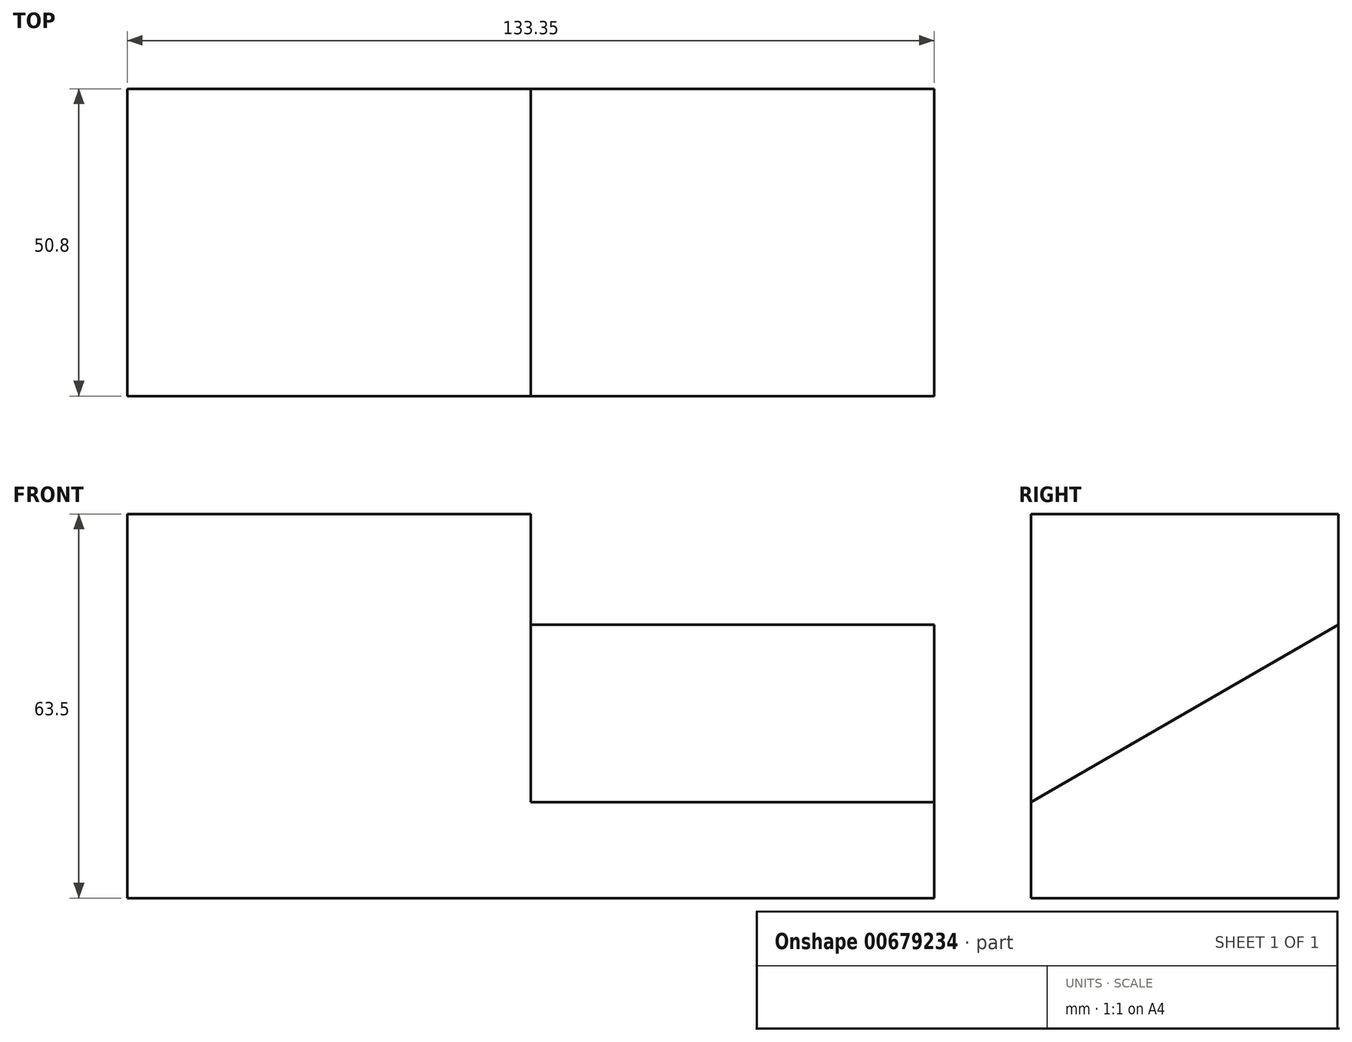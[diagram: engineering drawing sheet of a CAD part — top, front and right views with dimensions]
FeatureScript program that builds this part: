
annotation { "Feature Type Name" : "Feature", "Feature Type Description" : "" }
export const myFeature = defineFeature(function(context is Context, id is Id, definition is map)
    precondition{}
    {
        {
            var Q0;
            Q0=qCreatedBy(makeId("Front.planeOp"),FACE);
            var sketch = newSketch(context, id + "F0", { "sketchPlane" : qUnion([Q0])});
            skLineSegment(sketch, "E0.bottom", {"start": v(-33.34, 31.75) * mm, "end": v(33.34, 31.75) * mm});
            skLineSegment(sketch, "E0.top", {"start": v(-33.34, -31.75) * mm, "end": v(33.34, -31.75) * mm});
            skLineSegment(sketch, "E0.left", {"start": v(-33.34, 31.75) * mm, "end": v(-33.34, -31.75) * mm});
            skLineSegment(sketch, "E0.right", {"start": v(33.34, 31.75) * mm, "end": v(33.34, -31.75) * mm});
            skPoint(sketch, "E0.middle", {"position": v(0, 0) * mm});
            skSolve(sketch);
        }
        {
            var Q0;
            Q0=makeQuery(id+"F0.imprint","IMPRINT",FACE,{"disambiguationData":[TD([[makeQuery(id+"F0.imprint","IMPRINT",EDGE,{"derivedFrom":sQuery(id+"F0.wireOp",EDGE,"E0.bottom")}),-1.0]])]});
            extrude(context, id + "F1", {"entities" : qUnion([Q0]), "depth" : 50.8 * mm, "offsetDistance" : 25.4 * mm});
        }
        {
            var Q0;
            Q0=makeQuery(id+"F1.opExtrude","SWEPT_FACE",FACE,{"disambiguationData":[OSD([sQuery(id+"F0.wireOp",EDGE,"E0.right")])]});
            var sketch = newSketch(context, id + "F2", { "sketchPlane" : qUnion([Q0])});
            skLineSegment(sketch, "E1", {"start": v(-50.8, -31.75) * mm, "end": v(-50.8, -15.87) * mm});
            skLineSegment(sketch, "E2", {"start": v(-50.8, -15.88) * mm, "end": v(0, 13.45) * mm});
            skLineSegment(sketch, "E3", {"start": v(0, 13.45) * mm, "end": v(0, -31.75) * mm});
            skLineSegment(sketch, "E4", {"start": v(0, -31.75) * mm, "end": v(-50.8, -31.75) * mm});
            skSolve(sketch);
        }
        {
            var Q0;
            Q0=makeQuery(id+"F2.imprint","IMPRINT",FACE,{"disambiguationData":[TD([[makeQuery(id+"F2.imprint","IMPRINT",EDGE,{"derivedFrom":sQuery(id+"F2.wireOp",EDGE,"E1")}),1.0]])]});
            extrude(context, id + "F3", {"entities" : qUnion([Q0]), "operationType" : NewBodyOperationType.ADD, "depth" : 66.67 * mm, "offsetDistance" : 25.4 * mm});
        }
    });
